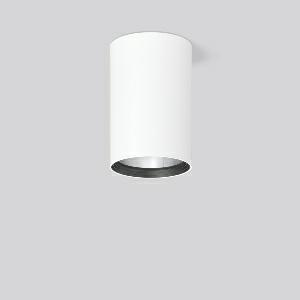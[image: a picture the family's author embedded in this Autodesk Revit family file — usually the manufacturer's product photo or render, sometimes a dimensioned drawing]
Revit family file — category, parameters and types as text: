
# Revit family: heledon_maxi_a_931218_002_2_76_f60e
name_source: partatom
category: Lighting Fixtures
units: mm (PartAtom-declared; Revit-internal decimal feet)

## family parameters
Cut with Voids When Loaded = No
Host = Face
Light Source = No
Part Type = Normal
Room Calculation Point = No
Round Connector Dimension = Use Diameter
Shared = No

## types (1)
- HELEDON maxi A (1 x LED Modul 927, 3150 lm, 2700)
    Apparent Load = 25 VA
    Approval mark = CE
    CIE Flux Codes = 100 100 100 100 100
    Color Rendering = 92
    Color Temperature = 2700
    Default Elevation = 1800 mm
    Description = Series: HELEDON maxi
Cylindrical surface-mounted downlight. Housing: die-cast aluminium, powder-coated. Internal ceiling frame polycarbonate with bayonet mounting. Black plastic ring and recessed LED to prevent glare from the side. Optical assembly with reflector made of MIRO-Silver with 98% total light reflection for outstanding efficiency - can be changed without tools. Best colour rendering index Ra>90. Suitable for Ceiling mounting. Easy installation with a separate ceiling frame with bayonet mounting and plug connection. Driver integrated. Connected via plug-in connector. High quality converter without flickering and stroboscopic effect. The following accessories can be mounted without use of tools: interchangeable lenses, decorative glasses, honeycomb louvre, clear and frosted diffusers, white interchangeable plastic ring. 
Colour: traffic white, matt (RAL 9016)
Diameter: 123 mm
Height: 183 mm
Lamp: LED
Socket: without socket
Colour temperature: 2700K
Colour rendering index (CRI): 92
System power: 25 W
Rated luminous flux: 3150 lm
Luminous efficiency: 126 lm/W
Control gear: Converter, dimmable, DALI
Protection class: I
Type of protection: IP 20
    Height = 183 mm
    Lamp = 1 x LED Modul 927
    Lamp Light Flux = 3150 lm
    Lamp count = 1
    Length = 123 mm
    Lifetime = 50000 h
    Luminous efficacy = 126 lm/W
    Manufacturer = RZB
    ModVariant = No
    Model = 931218.002.2.76
    Mounting Place = Ceiling
    Mounting Type = Surface mounted
    Number of Poles = 1
    OnlyDefault = Yes
    Power Factor = 1
    Product Name = HELEDON maxi A
    Product group = Surface mounted downlights
    ProductGroupID = 302
    Protection Class = Protection class I
    Protection Degree = IP 20
    RLX_Detail_Level = 1
    RLX_Emergency_Light_Flux = 0 lm
    RLX_Emergency_Type = 0
    RLX_Emergency_Type_DB = No
    RlxData = <blob elided: 99553 chars, md5=44639cd9>
    Socket = socket
    Standby Power = 0 W
    System Light Flux = 3150 lm
    System Power = 25 W
    Type Comments = Product without accessories
    Type Image = 931192.002.jpg
    URL = http://relux.com
    VarID = ---
    Voltage = 230 V
    Voltage Range = 220-240 V
    Weight = 0.00 kg
    Width = 0 mm  [stored 0 ft]

note: [stored X ft] marks values corroborated as IEEE doubles in the binary element streams (Revit-internal decimal feet)

## geometry (parser evidence)
native form markers: Blend x4, Sweep x9
no freeform markers — native parametric forms only
